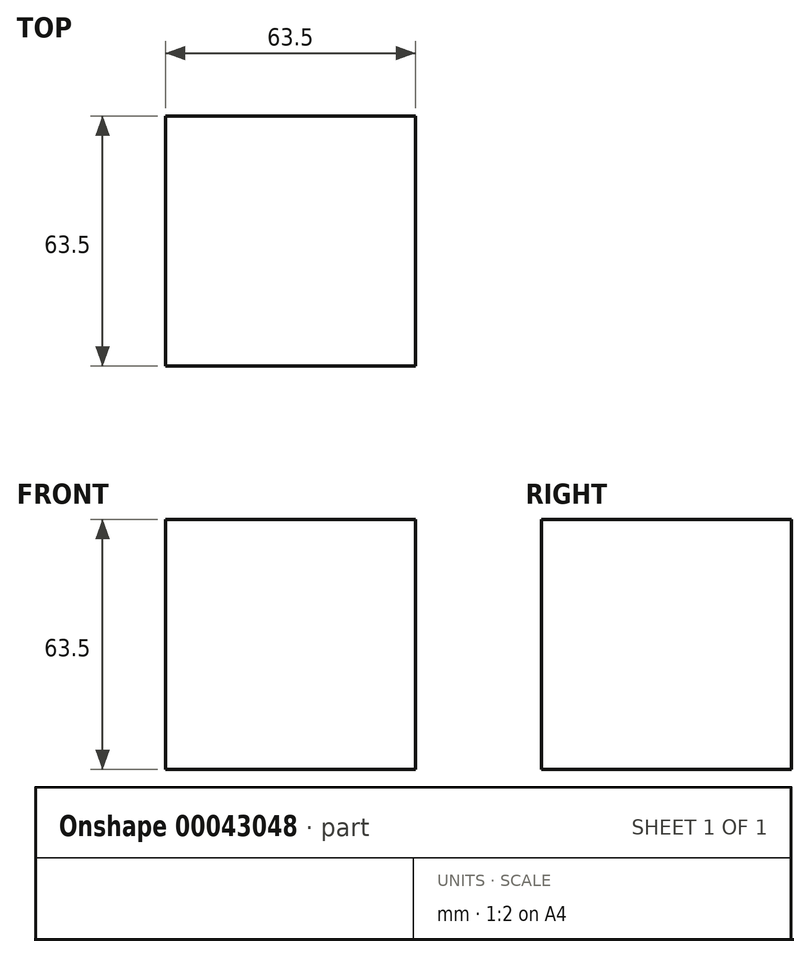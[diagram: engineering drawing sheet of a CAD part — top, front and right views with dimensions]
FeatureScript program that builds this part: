
annotation { "Feature Type Name" : "Feature", "Feature Type Description" : "" }
export const myFeature = defineFeature(function(context is Context, id is Id, definition is map)
    precondition{}
    {
        {
            var Q0;
            Q0=qCreatedBy(makeId("Front.planeOp"),FACE);
            var sketch = newSketch(context, id + "F0", { "sketchPlane" : qUnion([Q0])});
            skLineSegment(sketch, "E0.bottom", {"start": v(-36.66, 41.4) * mm, "end": v(26.84, 41.4) * mm});
            skLineSegment(sketch, "E0.top", {"start": v(-36.66, -22.1) * mm, "end": v(26.84, -22.1) * mm});
            skLineSegment(sketch, "E0.left", {"start": v(-36.66, 41.4) * mm, "end": v(-36.66, -22.1) * mm});
            skLineSegment(sketch, "E0.right", {"start": v(26.84, 41.4) * mm, "end": v(26.84, -22.1) * mm});
            skSolve(sketch);
        }
        {
            var Q0;
            Q0 = qSketchRegion(id + "F0", true);
            extrude(context, id + "F1", {"entities" : qUnion([Q0]), "depth" : 63.5 * mm});
        }
    });
